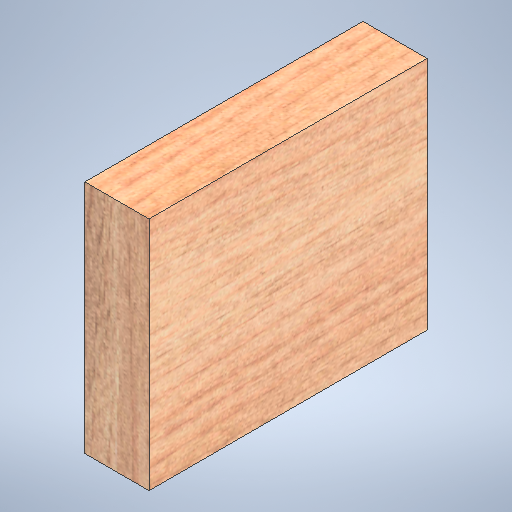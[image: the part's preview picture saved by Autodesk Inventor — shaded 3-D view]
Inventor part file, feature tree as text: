
AUTODESK INVENTOR PART (.ipt)
format: ipt  version: 2025 (Build 290162010, 162A)  size: 477,696 bytes
history: native  units: in
note: dims shown in document units (in); Inventor stores cm internally (conversion verified against a paired STEP export)
features: extrude x1, sketch x1
ambient origin geometry x8: Origin, YZ Plane, XZ Plane, XY Plane, X Axis, Y Axis, Z Axis, Center Point
bodies: Solid1 (feature_tree)
feature tree (2):
  extrude  "Extrusion1"  Depth=5.5in
  sketch  "Sketch1"  dims[d0=1.5in d1=5.5in d2=6.5in d3=0.0in]
